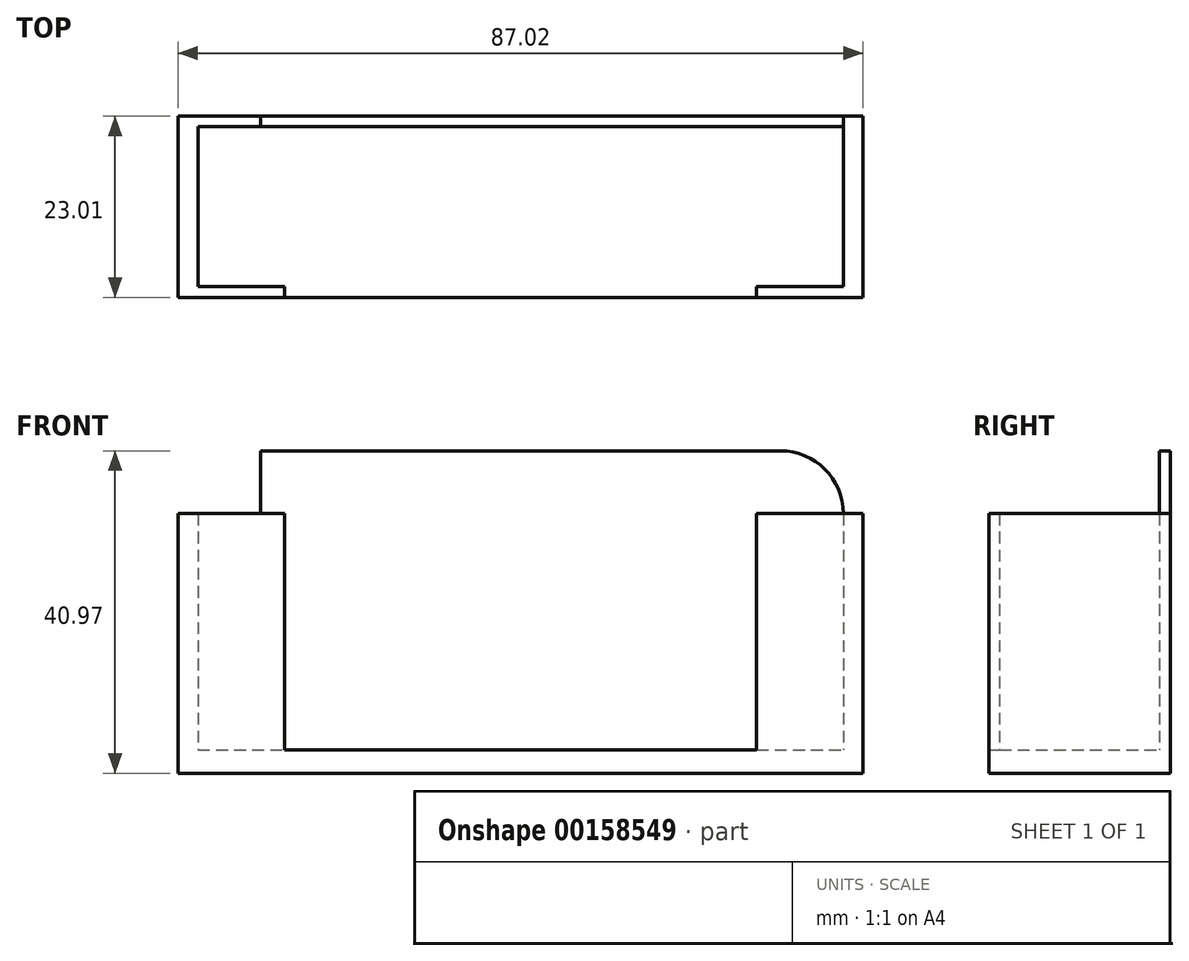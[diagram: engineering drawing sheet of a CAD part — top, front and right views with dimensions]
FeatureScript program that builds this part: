
annotation { "Feature Type Name" : "Feature", "Feature Type Description" : "" }
export const myFeature = defineFeature(function(context is Context, id is Id, definition is map)
    precondition{}
    {
        {
            var Q0;
            Q0=qCreatedBy(makeId("Top.planeOp"),FACE);
            var sketch = newSketch(context, id + "F0", { "sketchPlane" : qUnion([Q0])});
            skLineSegment(sketch, "E0", {"start": v(0, 11.5) * mm, "end": v(-43.51, 11.5) * mm});
            skLineSegment(sketch, "E1", {"start": v(0, -11.5) * mm, "end": v(43.51, -11.5) * mm});
            skLineSegment(sketch, "E2.bottom", {"start": v(-43.51, 11.5) * mm, "end": v(43.51, 11.5) * mm});
            skLineSegment(sketch, "E2.top", {"start": v(-43.51, -11.5) * mm, "end": v(43.51, -11.5) * mm});
            skLineSegment(sketch, "E2.left", {"start": v(-43.51, 11.5) * mm, "end": v(-43.51, -11.5) * mm});
            skLineSegment(sketch, "E2.right", {"start": v(43.51, 11.5) * mm, "end": v(43.51, -11.5) * mm});
            skSolve(sketch);
        }
        {
            var Q0;
            {var subQ0=sQuery(id+"F0.wireOp",EDGE,"E2.left");Q0=makeQuery(id+"F0.imprint","IMPRINT",FACE,{"disambiguationData":[TD([[makeQuery(id+"F0.imprint","IMPRINT",EDGE,{"derivedFrom":subQ0}),1.0]])]});}
            extrude(context, id + "F1", {"entities" : qUnion([Q0]), "depth" : 3 * mm});
        }
        {
            var Q0;
            Q0=makeQuery(id+"F1.opExtrude","CAP_FACE",FACE,{"disambiguationData":[OSD([sQuery(id+"F0.wireOp",EDGE,"E2.bottom"),sQuery(id+"F0.wireOp",EDGE,"E2.top"),sQuery(id+"F0.wireOp",EDGE,"E2.left"),sQuery(id+"F0.wireOp",EDGE,"E2.right")])],"isStart":false});
            var sketch = newSketch(context, id + "F2", { "sketchPlane" : qUnion([Q0])});
            skLineSegment(sketch, "E3", {"start": v(0.02, -10.17) * mm, "end": v(-40.97, -10.17) * mm});
            skLineSegment(sketch, "E4", {"start": v(0, 10.16) * mm, "end": v(40.99, 10.16) * mm});
            skLineSegment(sketch, "E5.bottom", {"start": v(-40.97, -10.17) * mm, "end": v(40.99, -10.17) * mm});
            skLineSegment(sketch, "E5.top", {"start": v(-40.97, 10.16) * mm, "end": v(40.99, 10.16) * mm});
            skLineSegment(sketch, "E5.left", {"start": v(-40.97, -10.17) * mm, "end": v(-40.97, 10.16) * mm});
            skLineSegment(sketch, "E5.right", {"start": v(40.99, -10.17) * mm, "end": v(40.99, 10.16) * mm});
            skLineSegment(sketch, "E6", {"start": v(0, 11.5) * mm, "end": v(-43.51, 11.5) * mm});
            skLineSegment(sketch, "E7", {"start": v(0, -11.5) * mm, "end": v(43.51, -11.5) * mm});
            skLineSegment(sketch, "E8.bottom", {"start": v(-43.51, 11.5) * mm, "end": v(43.51, 11.5) * mm});
            skLineSegment(sketch, "E8.top", {"start": v(-43.51, -11.5) * mm, "end": v(43.51, -11.5) * mm});
            skLineSegment(sketch, "E8.left", {"start": v(-43.51, 11.5) * mm, "end": v(-43.51, -11.5) * mm});
            skLineSegment(sketch, "E8.right", {"start": v(43.51, 11.5) * mm, "end": v(43.51, -11.5) * mm});
            skLineSegment(sketch, "E9", {"start": v(0, -11.5) * mm, "end": v(-30, -11.5) * mm});
            skLineSegment(sketch, "E10", {"start": v(0, -11.5) * mm, "end": v(24.46, -11.5) * mm});
            skLineSegment(sketch, "E11", {"start": v(0, -11.5) * mm, "end": v(30, -11.5) * mm});
            skLineSegment(sketch, "E12", {"start": v(-30, -11.5) * mm, "end": v(-30, -10.17) * mm});
            skLineSegment(sketch, "E13", {"start": v(30, -11.5) * mm, "end": v(30, -10.17) * mm});
            skSolve(sketch);
        }
        {
            var Q0;
            {var subQ1=sQuery(id+"F2.wireOp",EDGE,"E9");Q0=makeQuery(id+"F2.imprint","IMPRINT",FACE,{"disambiguationData":[TD([[makeQuery(id+"F2.imprint","IMPRINT",EDGE,{"derivedFrom":subQ1}),1.0]])]});}
            var Q1;
            {var subQ6=sQuery(id+"F2.wireOp",EDGE,"E5.left");Q1=makeQuery(id+"F2.imprint","IMPRINT",FACE,{"disambiguationData":[TD([[makeQuery(id+"F2.imprint","IMPRINT",EDGE,{"derivedFrom":subQ6}),1.0]])]});}
            extrude(context, id + "F3", {"entities" : qUnion([Q0, Q1]), "operationType" : NewBodyOperationType.ADD, "depth" : 30 * mm});
        }
        {
            var Q0;
            Q0=makeQuery(id+"F3.opExtrude","CAP_FACE",FACE,{"disambiguationData":[OSD([sQuery(id+"F2.wireOp",EDGE,"E5.bottom"),sQuery(id+"F2.wireOp",EDGE,"E5.top"),sQuery(id+"F2.wireOp",EDGE,"E5.left"),sQuery(id+"F2.wireOp",EDGE,"E5.right"),sQuery(id+"F2.wireOp",EDGE,"E8.bottom"),sQuery(id+"F2.wireOp",EDGE,"E8.top"),sQuery(id+"F2.wireOp",EDGE,"E8.left"),sQuery(id+"F2.wireOp",EDGE,"E8.right"),sQuery(id+"F2.wireOp",EDGE,"E9"),sQuery(id+"F2.wireOp",EDGE,"E11")])],"isStart":false});
            var sketch = newSketch(context, id + "F4", { "sketchPlane" : qUnion([Q0])});
            skLineSegment(sketch, "E14", {"start": v(0, 10.16) * mm, "end": v(-33, 10.16) * mm});
            skLineSegment(sketch, "E15", {"start": v(-33, 10.16) * mm, "end": v(33.03, 10.16) * mm});
            skLineSegment(sketch, "E16", {"start": v(-33, 10.16) * mm, "end": v(-33, 11.5) * mm});
            skLineSegment(sketch, "E17", {"start": v(-33, 11.5) * mm, "end": v(33.03, 11.5) * mm});
            skLineSegment(sketch, "E18", {"start": v(33.03, 11.5) * mm, "end": v(33.03, 10.16) * mm});
            skSolve(sketch);
        }
        {
            var Q0;
            {var subQ0=sQuery(id+"F4.wireOp",EDGE,"E16");Q0=makeQuery(id+"F4.imprint","IMPRINT",FACE,{"disambiguationData":[TD([[makeQuery(id+"F4.imprint","IMPRINT",EDGE,{"derivedFrom":subQ0}),-1.0]])]});}
            extrude(context, id + "F5", {"entities" : qUnion([Q0]), "operationType" : NewBodyOperationType.ADD, "depth" : 7.97 * mm});
        }
        {
            var Q0;
            Q0=makeQuery(id+"F5.boolean.opBoolean","MERGE",FACE,{"derivedFrom":[makeQuery(id+"F3.opExtrude","SWEPT_FACE",FACE,{"disambiguationData":[OSD([sQuery(id+"F2.wireOp",EDGE,"E5.top")])]}),makeQuery(id+"F5.opExtrude","SWEPT_FACE",FACE,{"disambiguationData":[OSD([sQuery(id+"F4.wireOp",EDGE,"E15")])]})]});
            var sketch = newSketch(context, id + "F6", { "sketchPlane" : qUnion([Q0])});
            skArc(sketch, "E19", {"start": v(-40.97, 33) * mm, "mid": v(-38.64, 38.63) * mm, "end": v(-33, 40.96) * mm});
            skArc(sketch, "E20", {"start": v(40.99, 33) * mm, "mid": v(38.66, 38.63) * mm, "end": v(33.03, 40.96) * mm});
            skSolve(sketch);
        }
        {
            var Q0;
            {var subQ0=sQuery(id+"F6.wireOp",EDGE,"E19");Q0=makeQuery(id+"F6.imprint","IMPRINT",FACE,{"disambiguationData":[TD([[makeQuery(id+"F6.imprint","IMPRINT",EDGE,{"derivedFrom":subQ0}),-1.0]])]});}
            var Q1;
            {var subQ0=sQuery(id+"F6.wireOp",EDGE,"E20");Q1=makeQuery(id+"F6.imprint","IMPRINT",FACE,{"disambiguationData":[TD([[makeQuery(id+"F6.imprint","IMPRINT",EDGE,{"derivedFrom":subQ0}),1.0]])]});}
            extrude(context, id + "F7", {"entities" : qUnion([Q0, Q1]), "operationType" : NewBodyOperationType.ADD, "oppositeDirection" : true, "depth" : 1.35 * mm});
        }
    });
